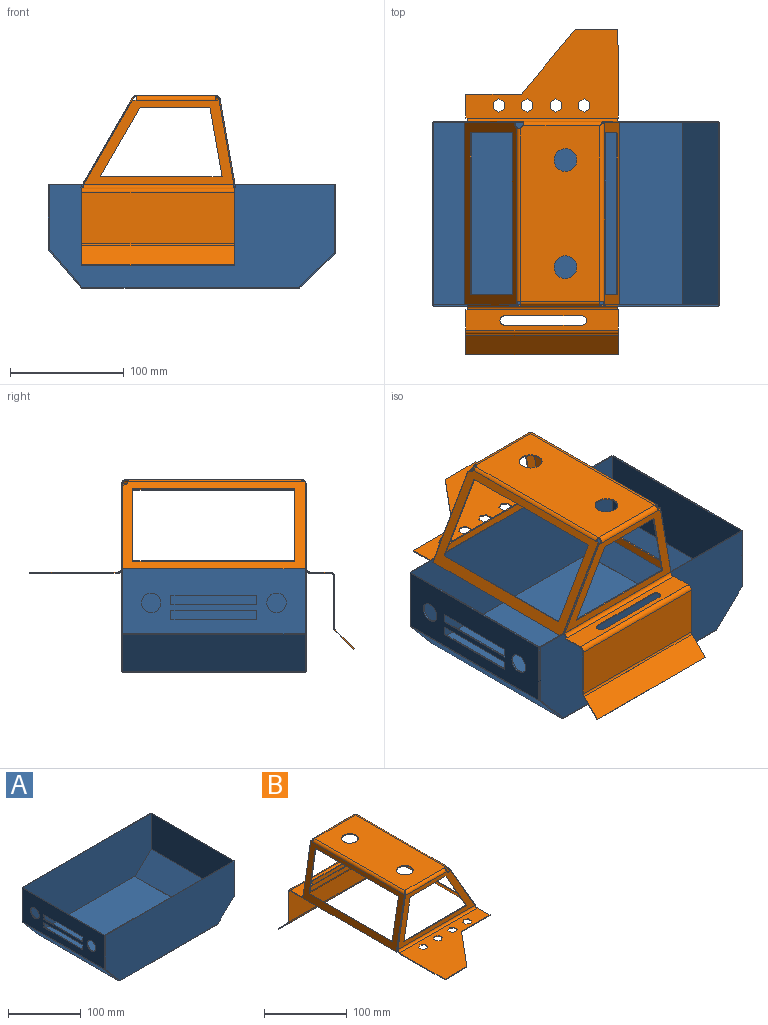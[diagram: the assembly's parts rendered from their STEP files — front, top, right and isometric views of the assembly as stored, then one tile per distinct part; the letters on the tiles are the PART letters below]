
ASSEMBLY  parts=2 mates=1
PART A: 76 faces, bbox 252x162x91 mm
  f0: plane 1x0.12mm, normal (0,0,-1), area 0.1mm2, adj f1,f7,f8,f65
  f1: plane 31.54x29.91mm, normal (0.69,0,-0.73), area 43.5mm2, adj f0,f6,f7,f8
  f2: plane 1x0.11mm, normal (0,0,-1), area 0.1mm2, adj f3,f7,f8,f64
  f3: plane 33.02x28.28mm, normal (-0.76,0,-0.65), area 43.5mm2, adj f2,f4,f7,f8
  f4: plane 56.88x1mm, normal (-1,0,0), area 56.9mm2, adj f3,f5,f7,f8
  f5: plane 249.96x1mm, normal (0,0,1), area 250mm2, adj f4,f6,f7,f8
  f6: plane 59.99x1mm, normal (1,0,0), area 60mm2, adj f1,f5,f7,f8
  f7: plane 249.96x89.9mm, normal (0,1,0), area 21532.8mm2, adj f0,f1,f2,f3,f4,f5,f6,f66
  f8: plane 249.96x89.9mm, normal (0,-1,0), area 21532.8mm2, adj f0,f1,f2,f3,f4,f5,f6,f67
  f9: plane 1x0.11mm, normal (0,0,-1), area 0.1mm2, adj f10,f16,f17,f60
  f10: plane 33.02x28.28mm, normal (-0.76,0,-0.65), area 43.5mm2, adj f9,f15,f16,f17
  f11: plane 1x0.12mm, normal (0,0,-1), area 0.1mm2, adj f12,f16,f17,f61
  f12: plane 31.54x29.91mm, normal (0.69,0,-0.73), area 43.5mm2, adj f11,f13,f16,f17
  f13: plane 59.99x1mm, normal (1,0,0), area 60mm2, adj f12,f14,f16,f17
  f14: plane 249.96x1mm, normal (0,0,1), area 250mm2, adj f13,f15,f16,f17
  f15: plane 56.88x1mm, normal (-1,0,0), area 56.9mm2, adj f10,f14,f16,f17
  f16: plane 249.96x89.9mm, normal (0,-1,0), area 21532.8mm2, adj f9,f10,f11,f12,f13,f14,f15,f62
  f17: plane 249.96x89.9mm, normal (0,1,0), area 21532.8mm2, adj f9,f10,f11,f12,f13,f14,f15,f63
  f18: plane 59.96x1mm, normal (0,-1,0), area 60mm2, adj f20,f21,f22,f73
  f19: plane 59.96x1mm, normal (0,1,0), area 60mm2, adj f20,f21,f22,f72
  f20: plane 159.96x1mm, normal (0,0,1), area 160mm2, adj f18,f19,f21,f22
  f21: plane 159.96x59.96mm, normal (1,0,0), area 9590.7mm2, adj f18,f19,f20,f74
  f22: plane 159.96x59.96mm, normal (-1,0,0), area 9590.7mm2, adj f18,f19,f20,f75
  f23: plane 0.73x0.69mm, normal (-0.73,0,-0.69), area 0.1mm2, adj f24,f27,f28,f69
  f24: plane 32.27x30.67mm, normal (0,-1,0), area 43.5mm2, adj f23,f27,f28,f73
  f25: plane 0.73x0.69mm, normal (-0.73,0,-0.69), area 0.1mm2, adj f26,f27,f28,f68
  f26: plane 32.27x30.67mm, normal (0,1,0), area 43.5mm2, adj f25,f27,f28,f72
  f27: plane 159.96x31.58mm, normal (0.69,0,-0.73), area 6961mm2, adj f23,f24,f25,f26,f70,f74
  f28: plane 159.96x31.58mm, normal (-0.69,0,0.73), area 6961mm2, adj f23,f24,f25,f26,f71,f75
  f29: plane 189.91x159.8mm, normal (0,0,-1), area 30348.3mm2, adj f58,f62,f66,f70
  f30: plane 189.91x159.8mm, normal (0,0,1), area 30348.3mm2, adj f59,f63,f67,f71
  f31: plane 0.76x0.65mm, normal (0.65,0,-0.76), area 0.1mm2, adj f33,f35,f36,f56
  f32: plane 33.7x29.07mm, normal (0,-1,0), area 43.5mm2, adj f34,f35,f36,f53
  f33: plane 33.7x29.07mm, normal (0,1,0), area 43.5mm2, adj f31,f35,f36,f52
  f34: plane 0.76x0.65mm, normal (0.65,0,-0.76), area 0.1mm2, adj f32,f35,f36,f57
  f35: plane 159.96x33.05mm, normal (-0.76,0,-0.65), area 6961mm2, adj f31,f32,f33,f34,f54,f58
  f36: plane 159.96x33.05mm, normal (0.76,0,0.65), area 6961mm2, adj f31,f32,f33,f34,f55,f59
  f37: plane 8x1mm, normal (0,1,0), area 8mm2, adj f38,f49,f50,f51
  f38: plane 75.3x1mm, normal (0,0,1), area 75.3mm2, adj f37,f39,f50,f51
  f39: plane 8x1mm, normal (0,-1,0), area 8mm2, adj f38,f49,f50,f51
  f40: plane 8x1mm, normal (0,1,0), area 8mm2, adj f41,f48,f50,f51
  f41: plane 75.3x1mm, normal (0,0,1), area 75.3mm2, adj f40,f42,f50,f51
  f42: plane 8x1mm, normal (0,-1,0), area 8mm2, adj f41,f48,f50,f51
  f43: plane 56.85x1mm, normal (0,-1,0), area 56.8mm2, adj f44,f50,f51,f53
  f44: plane 159.96x1mm, normal (0,0,1), area 160mm2, adj f43,f45,f50,f51
  f45: plane 56.85x1mm, normal (0,1,0), area 56.8mm2, adj f44,f50,f51,f52
  f46: cylinder r=8.5mm len=17mm, axis (-1,0,0), area 53.4mm2, adj f50,f51
  f47: cylinder r=8.5mm len=17mm, axis (-1,0,0), area 53.4mm2, adj f50,f51
  f48: plane 75.3x1mm, normal (0,0,-1), area 75.3mm2, adj f40,f42,f50,f51
  f49: plane 75.3x1mm, normal (0,0,-1), area 75.3mm2, adj f37,f39,f50,f51
  f50: plane 159.96x56.85mm, normal (-1,0,0), area 7434.7mm2, adj f37,f38,f39,f40,f41,f42,f43,f44
  f51: plane 159.96x56.85mm, normal (1,0,0), area 7434.7mm2, adj f37,f38,f39,f40,f41,f42,f43,f44
  f52: plane 1.02x0.72mm, normal (0,1,0), area 0.4mm2, adj f33,f45,f54,f55
  f53: plane 1.02x0.72mm, normal (0,-1,0), area 0.4mm2, adj f32,f43,f54,f55
  f54: cylinder r=1.1mm len=159.96mm, axis (0,1,0), area 124.6mm2, adj f35,f50,f52,f53
  f55: cylinder r=0.1mm len=159.96mm, axis (0,1,0), area 11.3mm2, adj f36,f51,f52,f53
  f56: plane 1.04x0.84mm, normal (0,1,0), area 0.5mm2, adj f31,f58,f59,f64
  f57: plane 1.04x0.84mm, normal (0,-1,0), area 0.5mm2, adj f34,f58,f59,f60
  f58: cylinder r=1.1mm len=159.8mm, axis (0,1,0), area 151.6mm2, adj f29,f35,f56,f57
  f59: cylinder r=0.1mm len=159.8mm, axis (0,1,0), area 13.8mm2, adj f30,f36,f56,f57
  f60: plane 1.1x1.1mm, normal (-1,0,0), area 0.9mm2, adj f9,f57,f62,f63
  f61: plane 1.1x1.1mm, normal (1,0,0), area 0.9mm2, adj f11,f62,f63,f69
  f62: cylinder r=1.1mm len=189.91mm, axis (-1,0,0), area 328.1mm2, adj f16,f29,f60,f61
  f63: cylinder r=0.1mm len=189.91mm, axis (-1,0,0), area 29.8mm2, adj f17,f30,f60,f61
  f64: plane 1.1x1.1mm, normal (-1,0,0), area 0.9mm2, adj f2,f56,f66,f67
  f65: plane 1.1x1.1mm, normal (1,0,0), area 0.9mm2, adj f0,f66,f67,f68
  f66: cylinder r=1.1mm len=189.91mm, axis (-1,0,0), area 328.1mm2, adj f7,f29,f64,f65
  f67: cylinder r=0.1mm len=189.91mm, axis (-1,0,0), area 29.8mm2, adj f8,f30,f64,f65
  f68: plane 1.03x0.76mm, normal (0,1,0), area 0.5mm2, adj f25,f65,f70,f71
  f69: plane 1.03x0.76mm, normal (0,-1,0), area 0.5mm2, adj f23,f61,f70,f71
  f70: cylinder r=1.1mm len=159.8mm, axis (0,1,0), area 133.4mm2, adj f27,f29,f68,f69
  f71: cylinder r=0.1mm len=159.8mm, axis (0,1,0), area 12.1mm2, adj f28,f30,f68,f69
  f72: plane 1.03x0.8mm, normal (0,1,0), area 0.5mm2, adj f19,f26,f74,f75
  f73: plane 1.03x0.8mm, normal (0,-1,0), area 0.5mm2, adj f18,f24,f74,f75
  f74: cylinder r=1.1mm len=159.96mm, axis (0,1,0), area 142.9mm2, adj f21,f27,f72,f73
  f75: cylinder r=0.1mm len=159.96mm, axis (0,1,0), area 13mm2, adj f22,f28,f72,f73
PART B: 131 faces, bbox 135.9x285.2x149.1 mm
  f0: plane 154x69.74mm, normal (0,0,1), area 10109.7mm2, adj f2,f3,f4,f5,f55,f100,f115,f129
  f1: plane 154x69.74mm, normal (0,0,-1), area 10109.7mm2, adj f2,f3,f4,f5,f56,f101,f116,f130
  f2: cylinder r=10mm len=20mm, axis (0,0,-1), area 62.8mm2, adj f0,f1
  f3: cylinder r=10mm len=20mm, axis (0,0,-1), area 62.8mm2, adj f0,f1
  f4: plane 1x0.02mm, normal (-0.66,-0.75,0), area 0mm2, adj f0,f1,f53,f127
  f5: cylinder r=4.89mm len=2.26mm, axis (0,0,-1), area 3mm2, adj f0,f1,f54,f114
  f6: plane 72.5x41.69mm, normal (0.87,0,0.5), area 83.6mm2, adj f7,f13,f14,f49
  f7: plane 131.71x74mm, normal (0,-1,0), area 2551.8mm2, adj f6,f8,f9,f10,f11,f12,f14,f52
  f8: plane 106.98x1mm, normal (0,0,1), area 107mm2, adj f7,f9,f11,f13
  f9: plane 61x10.68mm, normal (0.99,0,-0.17), area 61.9mm2, adj f7,f8,f10,f13
  f10: plane 61.23x1mm, normal (0,0,-1), area 61.2mm2, adj f7,f9,f11,f13
  f11: plane 61x35.08mm, normal (-0.87,0,-0.5), area 70.4mm2, adj f7,f8,f10,f13
  f12: plane 74x12.95mm, normal (-0.99,0,0.17), area 75.1mm2, adj f7,f13,f50,f53
  f13: plane 131.71x74mm, normal (0,1,0), area 2551.8mm2, adj f6,f8,f9,f10,f11,f12,f14,f51
  f14: cylinder r=4.89mm len=6.56mm, axis (0,1,0), area 7.4mm2, adj f6,f7,f13,f54
  f15: plane 1x0.53mm, normal (0,1,0), area 0.5mm2, adj f46,f47,f48,f50
  f16: plane 56.78x1mm, normal (-1,-0.01,0), area 56.8mm2, adj f17,f46,f47,f48
  f17: plane 37.49x1mm, normal (0.01,-1,0), area 37.5mm2, adj f16,f18,f47,f48
  f18: plane 56.44x47.29mm, normal (0.77,-0.64,0), area 73.6mm2, adj f17,f19,f47,f48
  f19: plane 48.65x1mm, normal (0,-1,0), area 48.7mm2, adj f18,f20,f47,f48
  f20: plane 21x1mm, normal (1,0,0), area 21mm2, adj f19,f21,f47,f48
  f21: plane 1.73x1mm, normal (0,1,0), area 1.7mm2, adj f20,f47,f48,f49
  f22: plane 5x2.89mm, normal (0.5,0.87,0), area 5.8mm2, adj f23,f45,f47,f48
  f23: plane 5.77x1mm, normal (1,0,0), area 5.8mm2, adj f22,f24,f47,f48
  f24: plane 5x2.89mm, normal (0.5,-0.87,0), area 5.8mm2, adj f23,f25,f47,f48
  f25: plane 5x2.89mm, normal (-0.5,-0.87,0), area 5.8mm2, adj f24,f26,f47,f48
  f26: plane 5.77x1mm, normal (-1,0,0), area 5.8mm2, adj f25,f45,f47,f48
  f27: plane 5x2.89mm, normal (0.5,0.87,0), area 5.8mm2, adj f28,f44,f47,f48
  f28: plane 5.77x1mm, normal (1,0,0), area 5.8mm2, adj f27,f29,f47,f48
  f29: plane 5x2.89mm, normal (0.5,-0.87,0), area 5.8mm2, adj f28,f30,f47,f48
  f30: plane 5x2.89mm, normal (-0.5,-0.87,0), area 5.8mm2, adj f29,f31,f47,f48
  f31: plane 5.77x1mm, normal (-1,0,0), area 5.8mm2, adj f30,f44,f47,f48
  f32: plane 5x2.89mm, normal (0.5,0.87,0), area 5.8mm2, adj f33,f43,f47,f48
  f33: plane 5.77x1mm, normal (1,0,0), area 5.8mm2, adj f32,f34,f47,f48
  f34: plane 5x2.89mm, normal (0.5,-0.87,0), area 5.8mm2, adj f33,f35,f47,f48
  f35: plane 5x2.89mm, normal (-0.5,-0.87,0), area 5.8mm2, adj f34,f36,f47,f48
  f36: plane 5.77x1mm, normal (-1,0,0), area 5.8mm2, adj f35,f43,f47,f48
  f37: plane 5x2.89mm, normal (0.5,0.87,0), area 5.8mm2, adj f38,f42,f47,f48
  f38: plane 5.77x1mm, normal (1,0,0), area 5.8mm2, adj f37,f39,f47,f48
  f39: plane 5x2.89mm, normal (0.5,-0.87,0), area 5.8mm2, adj f38,f40,f47,f48
  f40: plane 5x2.89mm, normal (-0.5,-0.87,0), area 5.8mm2, adj f39,f41,f47,f48
  f41: plane 5.77x1mm, normal (-1,0,0), area 5.8mm2, adj f40,f42,f47,f48
  f42: plane 5x2.89mm, normal (-0.5,0.87,0), area 5.8mm2, adj f37,f41,f47,f48
  f43: plane 5x2.89mm, normal (-0.5,0.87,0), area 5.8mm2, adj f32,f36,f47,f48
  f44: plane 5x2.89mm, normal (-0.5,0.87,0), area 5.8mm2, adj f27,f31,f47,f48
  f45: plane 5x2.89mm, normal (-0.5,0.87,0), area 5.8mm2, adj f22,f26,f47,f48
  f46: plane 21x1mm, normal (-1,0,0), area 21mm2, adj f15,f16,f47,f48
  f47: plane 133.96x77.78mm, normal (0,0,1), area 5938.3mm2, adj f15,f16,f17,f18,f19,f20,f21,f22
  f48: plane 133.96x77.78mm, normal (0,0,-1), area 5938.3mm2, adj f15,f16,f17,f18,f19,f20,f21,f22
  f49: plane 4x4mm, normal (1,0,0), area 5.5mm2, adj f6,f21,f51,f52
  f50: plane 4x4mm, normal (-1,0,0), area 5.5mm2, adj f12,f15,f51,f52
  f51: cylinder r=4mm len=131.71mm, axis (1,0,0), area 827.5mm2, adj f13,f48,f49,f50
  f52: cylinder r=3mm len=131.71mm, axis (1,0,0), area 620.7mm2, adj f7,f47,f49,f50
  f53: bspline ~4x4mm, area 6.4mm2, adj f4,f12,f55,f56
  f54: bspline ~4x4mm, area 5.8mm2, adj f5,f14,f55,f56
  f55: cylinder r=4mm len=70.51mm, axis (1,0,0), area 431.8mm2, adj f0,f7,f53,f54
  f56: cylinder r=3mm len=70.51mm, axis (1,0,0), area 323.8mm2, adj f1,f13,f53,f54
  f57: plane 3.03x1mm, normal (0,0,1), area 3mm2, adj f58,f65,f66,f99
  f58: plane 74x12.95mm, normal (-0.99,0,0.17), area 75.1mm2, adj f57,f65,f66,f94
  f59: plane 3.44x1mm, normal (0,0,1), area 3.4mm2, adj f64,f65,f66,f98
  f60: plane 61x10.68mm, normal (0.99,0,-0.17), area 61.9mm2, adj f61,f63,f65,f66
  f61: plane 106.98x1mm, normal (0,0,1), area 107mm2, adj f60,f62,f65,f66
  f62: plane 61x35.08mm, normal (-0.87,0,-0.5), area 70.4mm2, adj f61,f63,f65,f66
  f63: plane 61.23x1mm, normal (0,0,-1), area 61.2mm2, adj f60,f62,f65,f66
  f64: plane 74x42.55mm, normal (0.87,0,0.5), area 85.4mm2, adj f59,f65,f66,f95
  f65: plane 131.71x74mm, normal (0,1,0), area 2562.3mm2, adj f57,f58,f59,f60,f61,f62,f63,f64
  f66: plane 131.71x74mm, normal (0,-1,0), area 2562.3mm2, adj f57,f58,f59,f60,f61,f62,f63,f64
  f67: plane 1.73x1mm, normal (0,-1,0), area 1.7mm2, adj f74,f75,f76,f95
  f68: plane 18x1mm, normal (-1,0,0), area 18mm2, adj f69,f75,f76,f91
  f69: plane 1x0.53mm, normal (0,-1,0), area 0.5mm2, adj f68,f75,f76,f94
  f70: cylinder r=4mm len=8mm, axis (0,0,1), area 12.6mm2, adj f71,f73,f75,f76
  f71: plane 68.11x1mm, normal (0,1,0), area 68.1mm2, adj f70,f72,f75,f76
  f72: cylinder r=4mm len=8mm, axis (0,0,1), area 12.6mm2, adj f71,f73,f75,f76
  f73: plane 68.11x1mm, normal (0,-1,0), area 68.1mm2, adj f70,f72,f75,f76
  f74: plane 18x1mm, normal (1,0,0), area 18mm2, adj f67,f75,f76,f90
  f75: plane 133.96x18mm, normal (0,0,1), area 1816.1mm2, adj f67,f68,f69,f70,f71,f72,f73,f74
  f76: plane 133.96x18mm, normal (0,0,-1), area 1816.1mm2, adj f67,f68,f69,f70,f71,f72,f73,f74
  f77: plane 44.76x1mm, normal (-1,0,0), area 44.8mm2, adj f79,f80,f86,f91
  f78: plane 44.76x1mm, normal (1,0,0), area 44.8mm2, adj f79,f80,f87,f90
  f79: plane 133.96x44.76mm, normal (0,1,0), area 5995.5mm2, adj f77,f78,f89,f92
  f80: plane 133.96x44.76mm, normal (0,-1,0), area 5995.5mm2, adj f77,f78,f88,f93
  f81: plane 133.96x0.71mm, normal (0,0.71,-0.71), area 134mm2, adj f82,f83,f84,f85
  f82: plane 17.21x17.21mm, normal (-1,0,0), area 23.3mm2, adj f81,f84,f85,f86
  f83: plane 17.21x17.21mm, normal (1,0,0), area 23.3mm2, adj f81,f84,f85,f87
  f84: plane 133.96x16.51mm, normal (0,0.71,0.71), area 3127mm2, adj f81,f82,f83,f89
  f85: plane 133.96x16.51mm, normal (0,-0.71,-0.71), area 3127mm2, adj f81,f82,f83,f88
  f86: plane 2.83x1.88mm, normal (-1,0,0), area 2.7mm2, adj f77,f82,f88,f89
  f87: plane 2.83x1.88mm, normal (1,0,0), area 2.7mm2, adj f78,f83,f88,f89
  f88: cylinder r=4mm len=133.96mm, axis (-1,0,0), area 420.8mm2, adj f80,f85,f86,f87
  f89: cylinder r=3mm len=133.96mm, axis (-1,0,0), area 315.6mm2, adj f79,f84,f86,f87
  f90: plane 4x4mm, normal (1,0,0), area 5.5mm2, adj f74,f78,f92,f93
  f91: plane 4x4mm, normal (-1,0,0), area 5.5mm2, adj f68,f77,f92,f93
  f92: cylinder r=4mm len=133.96mm, axis (1,0,0), area 841.7mm2, adj f75,f79,f90,f91
  f93: cylinder r=3mm len=133.96mm, axis (1,0,0), area 631.3mm2, adj f76,f80,f90,f91
  f94: plane 4x4mm, normal (-1,0,0), area 5.5mm2, adj f58,f69,f96,f97
  f95: plane 4x4mm, normal (1,0,0), area 5.5mm2, adj f64,f67,f96,f97
  f96: cylinder r=4mm len=131.71mm, axis (-1,0,0), area 827.5mm2, adj f66,f76,f94,f95
  f97: cylinder r=3mm len=131.71mm, axis (-1,0,0), area 620.7mm2, adj f65,f75,f94,f95
  f98: plane 4x4mm, normal (1,0,0), area 5.5mm2, adj f59,f100,f101,f113
  f99: plane 4x4mm, normal (-1,0,0), area 5.5mm2, adj f57,f100,f101,f128
  f100: cylinder r=4mm len=69.74mm, axis (1,0,0), area 438.2mm2, adj f0,f65,f98,f99
  f101: cylinder r=3mm len=69.74mm, axis (1,0,0), area 328.7mm2, adj f1,f66,f98,f99
  f102: plane 2.98x0.87mm, normal (-0.5,0,0.87), area 3mm2, adj f107,f110,f111,f113
  f103: plane 76.33x44.47mm, normal (0,-1,0), area 87.5mm2, adj f108,f110,f111,f112
  f104: plane 142x0.87mm, normal (-0.5,0,0.87), area 142mm2, adj f105,f109,f110,f111
  f105: plane 64.66x37.76mm, normal (0,1,0), area 74mm2, adj f104,f106,f110,f111
  f106: plane 142x0.87mm, normal (0.5,0,-0.87), area 142mm2, adj f105,f109,f110,f111
  f107: plane 78.99x46mm, normal (0,1,0), area 90.5mm2, adj f102,f108,f110,f111
  f108: plane 159.96x0.87mm, normal (0.5,0,-0.87), area 160mm2, adj f103,f107,f110,f111
  f109: plane 64.66x37.76mm, normal (0,-1,0), area 74mm2, adj f104,f106,f110,f111
  f110: plane 159.96x78.5mm, normal (0.87,0,0.5), area 3962.9mm2, adj f102,f103,f104,f105,f106,f107,f108,f109
  f111: plane 159.96x78.5mm, normal (-0.87,0,-0.5), area 3962.9mm2, adj f102,f103,f104,f105,f106,f107,f108,f109
  f112: cylinder r=4.89mm len=4.81mm, axis (-0.87,0,-0.5), area 6.1mm2, adj f103,f110,f111,f114
  f113: plane 3.47x2.5mm, normal (0,1,0), area 3.7mm2, adj f98,f102,f115,f116
  f114: bspline ~3.47x2.5mm, area 3.8mm2, adj f5,f112,f115,f116
  f115: cylinder r=4mm len=152.17mm, axis (0,-1,0), area 638.5mm2, adj f0,f110,f113,f114
  f116: cylinder r=3mm len=152.17mm, axis (0,-1,0), area 478.9mm2, adj f1,f111,f113,f114
  f117: plane 142x0.99mm, normal (0.17,0,0.99), area 142mm2, adj f118,f124,f125,f126
  f118: plane 61.87x11.78mm, normal (0,-1,0), area 62.6mm2, adj f117,f119,f125,f126
  f119: plane 142x0.99mm, normal (-0.17,0,-0.99), area 142mm2, adj f118,f124,f125,f126
  f120: plane 77.69x14.55mm, normal (0,1,0), area 78.7mm2, adj f121,f123,f125,f126
  f121: plane 159.96x0.99mm, normal (-0.17,0,-0.99), area 160mm2, adj f120,f122,f125,f126
  f122: plane 77.69x14.55mm, normal (0,-1,0), area 78.7mm2, adj f121,f125,f126,f127
  f123: plane 2.98x0.99mm, normal (0.17,0,0.99), area 3mm2, adj f120,f125,f126,f128
  f124: plane 61.87x11.78mm, normal (0,1,0), area 62.6mm2, adj f117,f119,f125,f126
  f125: plane 159.96x77.52mm, normal (-0.99,0,0.17), area 3693.9mm2, adj f117,f118,f119,f120,f121,f122,f123,f124
  f126: plane 159.96x77.52mm, normal (0.99,0,-0.17), area 3693.9mm2, adj f117,f118,f119,f120,f121,f122,f123,f124
  f127: bspline ~3.94x3.48mm, area 5.9mm2, adj f4,f122,f129,f130
  f128: plane 3.94x3.48mm, normal (0,1,0), area 4.9mm2, adj f99,f123,f129,f130
  f129: cylinder r=4mm len=156.98mm, axis (0,-1,0), area 871.5mm2, adj f0,f125,f127,f128
  f130: cylinder r=3mm len=156.98mm, axis (0,-1,0), area 653.6mm2, adj f1,f126,f127,f128
PLACE A t=(1.04,157.07,-33.85)mm
PLACE B rot(axis=(0,0,-1),180deg) t=(90.56,157.07,43.15)mm
MATE fastened A.f7 <-> B.f7  axis (0,1,0) through (1.06,158.07,-33.85)mm
